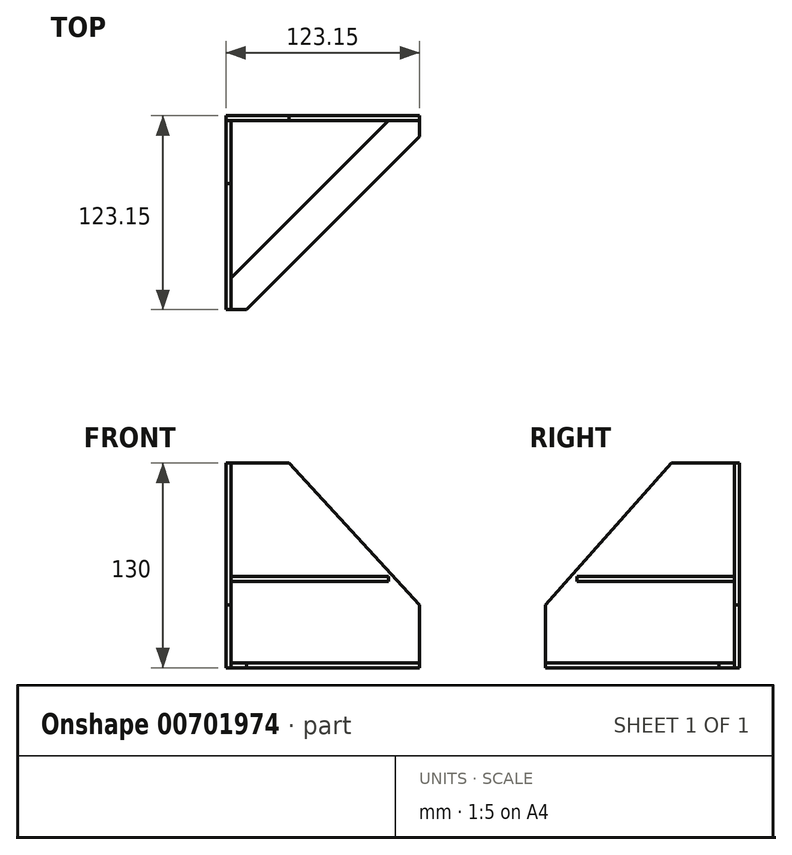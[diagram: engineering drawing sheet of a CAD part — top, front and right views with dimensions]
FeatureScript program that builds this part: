
annotation { "Feature Type Name" : "Feature", "Feature Type Description" : "" }
export const myFeature = defineFeature(function(context is Context, id is Id, definition is map)
    precondition{}
    {
        {
            assignVariable(context, id + "F0", {"name" : "x", "anyValue" : 3.15});
        }
        {
            var Q0;
            Q0=qCreatedBy(makeId("Top.planeOp"),FACE);
            var sketch = newSketch(context, id + "F1", { "sketchPlane" : qUnion([Q0])});
            skLineSegment(sketch, "E0.bottom", {"start": v(0, 0) * mm, "end": v(10, 0) * mm});
            skLineSegment(sketch, "E0.top", {"start": v(0, 120) * mm, "end": v(120, 120) * mm});
            skLineSegment(sketch, "E0.left", {"start": v(0, 0) * mm, "end": v(0, 120) * mm});
            skLineSegment(sketch, "E0.right", {"start": v(120, 110) * mm, "end": v(120, 120) * mm});
            skLineSegment(sketch, "E1", {"start": v(10, 0) * mm, "end": v(120, 110) * mm});
            skSolve(sketch);
        }
        {
            var Q0;
            Q0=qSketchRegion(id+"F1",true);
            extrude(context, id + "F2", {"entities" : qUnion([Q0]), "depth" : (getVariable(context, 'x')) * mm, "offsetDistance" : 25 * mm});
        }
        {
            var Q0;
            Q0=makeQuery(id+"F2.opExtrude","SWEPT_FACE",FACE,{"disambiguationData":[OSD([sQuery(id+"F1.wireOp",EDGE,"E0.left")])]});
            var sketch = newSketch(context, id + "F3", { "sketchPlane" : qUnion([Q0])});
            skLineSegment(sketch, "E2.top", {"start": v(-80, 130) * mm, "end": v(-120, 130) * mm});
            skLineSegment(sketch, "E2.left", {"start": v(0, 0) * mm, "end": v(0, 40) * mm});
            skLineSegment(sketch, "E3", {"start": v(0, 0) * mm, "end": v(-120, 0) * mm});
            skLineSegment(sketch, "E4", {"start": v(-120, 0) * mm, "end": v(-120, 130) * mm});
            skLineSegment(sketch, "E5", {"start": v(-80, 130) * mm, "end": v(0, 40) * mm});
            skSolve(sketch);
        }
        {
            var Q0;
            Q0=qSketchRegion(id+"F3",true);
            extrude(context, id + "F4", {"entities" : qUnion([Q0]), "depth" : (getVariable(context, 'x')) * mm, "offsetDistance" : 25 * mm});
        }
        {
            var Q0;
            Q0=makeQuery(id+"F2.opExtrude","SWEPT_FACE",FACE,{"disambiguationData":[OSD([sQuery(id+"F1.wireOp",EDGE,"E0.top")])]});
            var sketch = newSketch(context, id + "F5", { "sketchPlane" : qUnion([Q0])});
            skLineSegment(sketch, "E6.bottom", {"start": v(-120, 0) * mm, "end": v(3.15, 0) * mm});
            skLineSegment(sketch, "E6.top", {"start": v(-36.85, 130) * mm, "end": v(3.15, 130) * mm});
            skLineSegment(sketch, "E6.left", {"start": v(-120, 0) * mm, "end": v(-120, 40) * mm});
            skLineSegment(sketch, "E6.right", {"start": v(3.15, 0) * mm, "end": v(3.15, 130) * mm});
            skLineSegment(sketch, "E7", {"start": v(-36.85, 130) * mm, "end": v(-120, 40) * mm});
            skSolve(sketch);
        }
        {
            var Q0;
            Q0 = qSketchRegion(id + "F5", true);
            extrude(context, id + "F6", {"entities" : qUnion([Q0]), "depth" : (getVariable(context, 'x')) * mm, "offsetDistance" : 25 * mm});
        }
        {
            var Q0;
            Q0=makeQuery(id+"F2.opExtrude","CAP_FACE",FACE,{"disambiguationData":[OSD([sQuery(id+"F1.wireOp",EDGE,"E0.bottom"),sQuery(id+"F1.wireOp",EDGE,"E0.top"),sQuery(id+"F1.wireOp",EDGE,"E0.left"),sQuery(id+"F1.wireOp",EDGE,"E0.right"),sQuery(id+"F1.wireOp",EDGE,"E1")])],"isStart":false});
            cPlane(context, id + "F7", {"entities" : qUnion([Q0]), "cplaneType" : CPlaneType.OFFSET, "offset" : 55 * mm, "width" : 150 * mm, "height" : 150 * mm});
        }
        {
            var Q0;
            Q0=qCreatedBy(id+"F7.planeOp",FACE);
            var sketch = newSketch(context, id + "F8", { "sketchPlane" : qUnion([Q0])});
            skLineSegment(sketch, "E8", {"start": v(0, 20) * mm, "end": v(100, 120) * mm});
            skLineSegment(sketch, "E9", {"start": v(100, 120) * mm, "end": v(0, 120) * mm});
            skLineSegment(sketch, "E10", {"start": v(0, 120) * mm, "end": v(0, 20) * mm});
            skSolve(sketch);
        }
        {
            var Q0;
            Q0 = qSketchRegion(id + "F8", true);
            extrude(context, id + "F9", {"entities" : qUnion([Q0]), "oppositeDirection" : true, "depth" : (getVariable(context, 'x')) * mm, "offsetDistance" : 25 * mm});
        }
    });
